# Revit family: RN 90035 Optifitt-Serra-Tuyau
name_source: partatom
category: Rohrformteile
units: mm (PartAtom-declared; Revit-internal decimal feet)

## family parameters
Arbeitsebenenbasiert = Nein
Beim Laden mit Abzugskörper schneiden = Nein
Bemaßung runder Anschluss = Durchmesser verwenden
Gemeinsam genutzt = Nein
Immer vertikal = Ja
Teiletyp = Nicht definiert

## types (7) — shared parameters
1.010.00.2 Blattnummer der Richtlinie = 29
1.010.00.3 Ausgabedatum (Monat) der Richtlinie = 201308
1.010.00.4 Herstellername = R. Nussbaum AG
1.010.00.5 Revisionsdatum der Datei = 20190521
1.010.00.6 Webadresse des Herstellers = http://www.nussbaum.ch
1.100.00.4 Produktbezeichnung = Versorgung
1.110.00.2 Index = 3
1.110.00.4 Produktbezeichnung = Optifitt-Serra
1.960/3L.00.8 Link (URL) = https://www.nussbaum.ch
29.700.00.4 Produktname = Optifitt-Serra-Rohr, in Stangen
29.700.00.5 Produktkennung = 2
29.700.00.6 Querschnittsform = 1
29.700.00.7 Nennweitensystem = DN
29.700.00.8 Nenndrucksystem = PN
29.710.02.4 Nenndruck = 16
29.710.02.5 max. zul. Überdruck [hPa] = 1600
29.710.02.7 max. zul. Dauer-Betriebsdruck [hPa] = 1600
29.710.02.9 max. zul. Dauer-Betriebstemperatur [°C] = 90
CONNECTOR1_dX_01 = 3000 mm  [stored 9.84252 ft]
CONNECTOR1_ref_dX = 3000 mm  [stored 9.84252 ft]
Connector Visibility = Nein
EnclosingSpace Visibility = Nein
Hersteller = R. Nussbaum AG
URL = https://www.nussbaum.ch

## per-type parameters (varying)
| type | 1.800.00.3 TGA-Nummer | 1.800.00.4 Kommentarfeld | 1.810.00.3 Hersteller-Bestellnummer | 1.810.00.4 DATANORM-Nummer | 1.810.00.6 GTIN-Nummer | 29.710.02.10 Formstück-Gewicht [kg] | 29.710.02.3 Benennung | CONNECTOR0_DIAMETER_dX_0r | CONNECTOR0_dX_01 | CONNECTOR0_ref_dX | CONNECTOR1_DIAMETER_dX_0r | CONNECTOR1_dX_00 | Modell | R. Nussbaum AG 90035.04 de Visibility | R. Nussbaum AG 90035.05 de Visibility | R. Nussbaum AG 90035.06 de Visibility | R. Nussbaum AG 90035.07 de Visibility | R. Nussbaum AG 90035.08 de Visibility | R. Nussbaum AG 90035.09 de Visibility | R. Nussbaum AG 90035.10 de Visibility | Typenkommentare |
| DN=65 | 01900300000000000000000000000000000000000000000021000000000000000008 | 90035.10, Optifitt-Serra-Rohr, in Stangen, DN=65, L=3 | 90035.1 | 90035.1 | 7612945740915 | 10.892 | Optifitt-Serra-Rohr, in Stangen, DN=65, L=3 | 65 mm | 43 mm  [stored 0.141076 ft] | 43 mm  [stored 0.141076 ft] | 65 mm | 2957 mm | 90035.1 | Nein | Nein | Nein | Nein | Nein | Nein | Ja | Optifitt-Serra-Tuyau  DN=65 |
| DN=50 | 01900300000000000000000000000000000000000000000021000000000000000006 | 90035.09, Optifitt-Serra-Rohr, in Stangen, DN=50, L=3 | 90035.09 | 90035.09 | 7612945740908 | 7.374 | Optifitt-Serra-Rohr, in Stangen, DN=50, L=3 | 50 mm | 40 mm | 40 mm | 50 mm | 2960 mm | 90035.09 | Nein | Nein | Nein | Nein | Nein | Ja | Nein | Optifitt-Serra-Tuyau  DN=50 |
| DN=40 | 01900300000000000000000000000000000000000000000021000000000000000005 | 90035.08, Optifitt-Serra-Rohr, in Stangen, DN=40, L=3 | 90035.08 | 90035.08 | 7612945740496 | 5.038 | Optifitt-Serra-Rohr, in Stangen, DN=40, L=3 | 40 mm | 36 mm | 36 mm | 40 mm | 2964 mm | 90035.08 | Nein | Nein | Nein | Nein | Ja | Nein | Nein | Optifitt-Serra-Tuyau  DN=40 |
| DN=32 | 01900300000000000000000000000000000000000000000021000000000000000004 | 90035.07, Optifitt-Serra-Rohr, in Stangen, DN=32, L=3 | 90035.07 | 90035.07 | 7612945740489 | 4.535 | Optifitt-Serra-Rohr, in Stangen, DN=32, L=3 | 32 mm | 26 mm | 26 mm | 32 mm | 2974 mm | 90035.07 | Nein | Nein | Nein | Ja | Nein | Nein | Nein | Optifitt-Serra-Tuyau  DN=32 |
| DN=25 | 01900300000000000000000000000000000000000000000021000000000000000003 | 90035.06, Optifitt-Serra-Rohr, in Stangen, DN=25, L=3 | 90035.06 | 90035.06 | 7612945740472 | 3.363 | Optifitt-Serra-Rohr, in Stangen, DN=25, L=3 | 25 mm  [stored 0.082021 ft] | 24 mm | 24 mm | 25 mm  [stored 0.082021 ft] | 2976 mm | 90035.06 | Nein | Nein | Ja | Nein | Nein | Nein | Nein | Optifitt-Serra-Tuyau  DN=25 |
| DN=20 | 01900300000000000000000000000000000000000000000021000000000000000002 | 90035.05, Optifitt-Serra-Rohr, in Stangen, DN=20, L=3 | 90035.05 | 90035.05 | 7612945740465 | 2.415 | Optifitt-Serra-Rohr, in Stangen, DN=20, L=3 | 20 mm | 24 mm | 24 mm | 20 mm | 2976 mm | 90035.05 | Nein | Ja | Nein | Nein | Nein | Nein | Nein | Optifitt-Serra-Tuyau  DN=20 |
| DN=15 | 01900300000000000000000000000000000000000000000021000000000000000001 | 90035.04, Optifitt-Serra-Rohr, in Stangen, DN=15, L=3 | 90035.04 | 90035.04 | 7612945740458 | 1.844 | Optifitt-Serra-Rohr, in Stangen, DN=15, L=3 | 15 mm | 22 mm | 22 mm | 15 mm | 2978 mm | 90035.04 | Ja | Nein | Nein | Nein | Nein | Nein | Nein | Optifitt-Serra-Tuyau  DN=15 |

note: [stored X ft] marks values corroborated as IEEE doubles in the binary element streams (Revit-internal decimal feet)

## geometry (parser evidence)
native form markers: Sweep x2
no freeform markers — native parametric forms only
